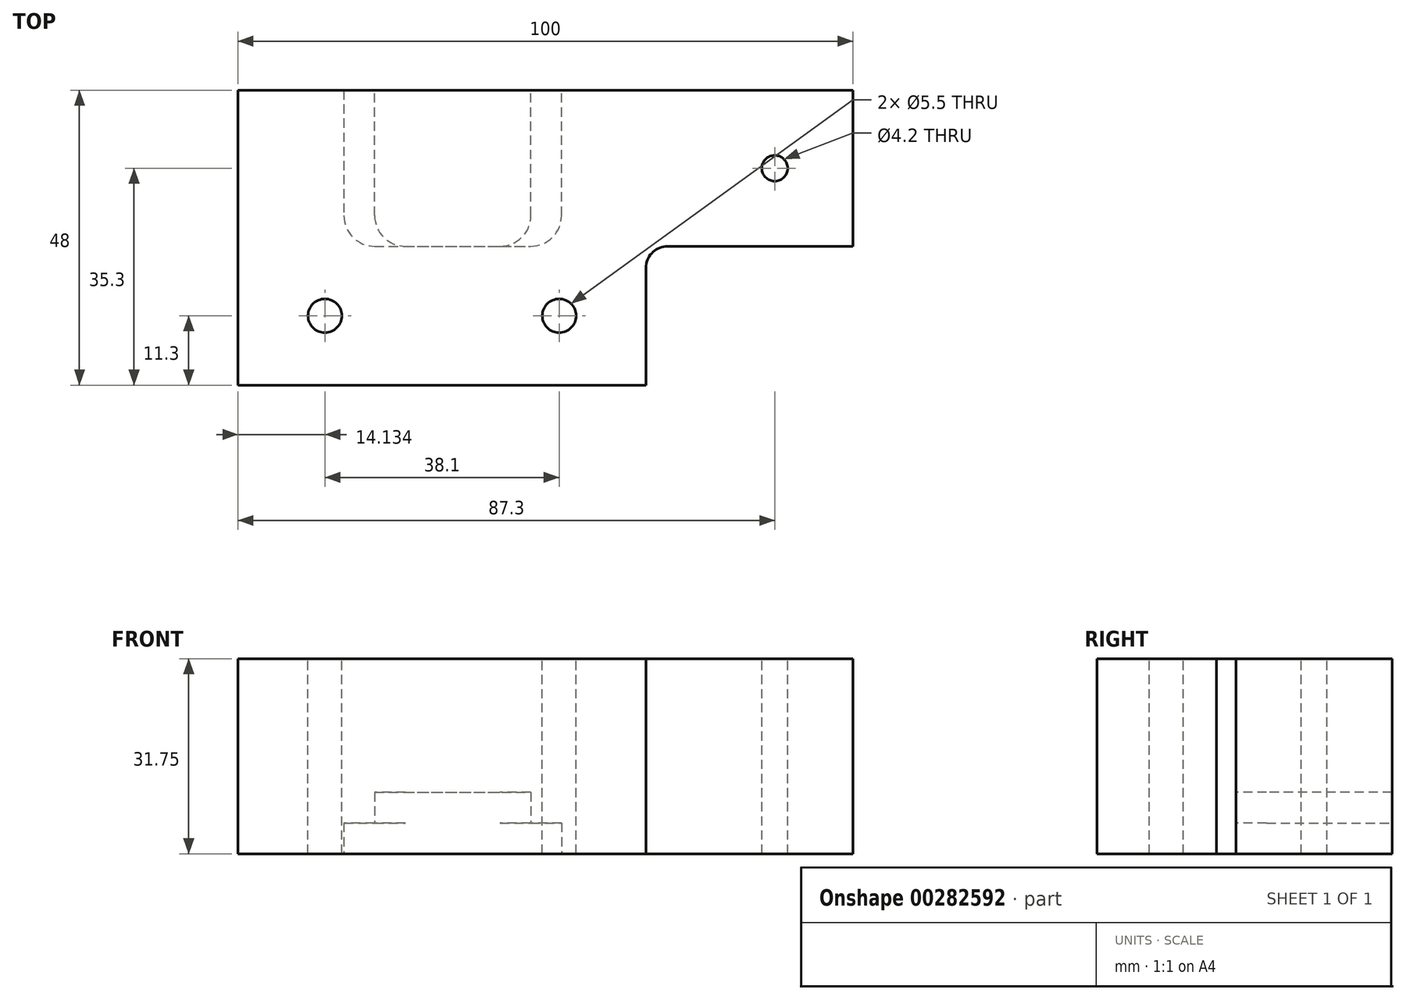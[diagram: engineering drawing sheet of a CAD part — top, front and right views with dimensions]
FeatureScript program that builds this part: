
annotation { "Feature Type Name" : "Feature", "Feature Type Description" : "" }
export const myFeature = defineFeature(function(context is Context, id is Id, definition is map)
    precondition{}
    {
        {
            var Q0;
            Q0=qCreatedBy(makeId("Top.planeOp"),FACE);
            var sketch = newSketch(context, id + "F0", { "sketchPlane" : qUnion([Q0])});
            skLineSegment(sketch, "E0.bottom", {"start": v(0, 0) * mm, "end": v(69.85, 0) * mm});
            skLineSegment(sketch, "E0.top", {"start": v(0, 48) * mm, "end": v(100, 48) * mm});
            skLineSegment(sketch, "E0.left", {"start": v(0, 0) * mm, "end": v(0, 48) * mm});
            skLineSegment(sketch, "E0.right", {"start": v(100, 22.6) * mm, "end": v(100, 48) * mm});
            skLineSegment(sketch, "E1", {"start": v(69.85, 22.6) * mm, "end": v(69.85, 0) * mm, "construction": true});
            skPoint(sketch, "E2.orphan", {"position": v(95.25, 0) * mm});
            skLineSegment(sketch, "E3", {"start": v(69.85, 22.6) * mm, "end": v(100, 22.6) * mm});
            skArc(sketch, "E4", {"start": v(69.85, 22.6) * mm, "mid": v(67.5, 21.7) * mm, "end": v(66.37, 19.45) * mm});
            skLineSegment(sketch, "E5", {"start": v(66.37, 19.45) * mm, "end": v(66.37, 0) * mm});
            skSolve(sketch);
        }
        {
            var Q0;
            Q0 = qSketchRegion(id + "F0", true);
            extrude(context, id + "F1", {"entities" : qUnion([Q0]), "depth" : 31.75 * mm});
        }
        {
            var Q0;
            Q0=makeQuery(id+"F1.opExtrude","CAP_FACE",FACE,{"disambiguationData":[OSD([sQuery(id+"F0.wireOp",EDGE,"E0.bottom"),sQuery(id+"F0.wireOp",EDGE,"E0.top"),sQuery(id+"F0.wireOp",EDGE,"E0.left"),sQuery(id+"F0.wireOp",EDGE,"E0.right"),sQuery(id+"F0.wireOp",EDGE,"ORaCKfpo-WbZt-Nzm5-LVTq-wue5MO5dMCIk"),sQuery(id+"F0.wireOp",EDGE,"E1")])],"isStart":true});
            var sketch = newSketch(context, id + "F2", { "sketchPlane" : qUnion([Q0])});
            skLineSegment(sketch, "E6.bottom", {"start": v(22.23, -48) * mm, "end": v(47.63, -48) * mm});
            skLineSegment(sketch, "E6.top", {"start": v(22.23, -22.6) * mm, "end": v(47.62, -22.6) * mm});
            skLineSegment(sketch, "E6.left", {"start": v(22.23, -48) * mm, "end": v(22.23, -22.6) * mm});
            skLineSegment(sketch, "E6.right", {"start": v(47.63, -48) * mm, "end": v(47.63, -22.6) * mm});
            skLineSegment(sketch, "E7", {"start": v(34.93, 0) * mm, "end": v(34.93, -48) * mm, "construction": true});
            skSolve(sketch);
        }
        {
            var Q0;
            Q0 = qSketchRegion(id + "F2", true);
            extrude(context, id + "F3", {"entities" : qUnion([Q0]), "operationType" : NewBodyOperationType.REMOVE, "oppositeDirection" : true, "depth" : 10 * mm});
        }
        {
            var Q0;
            Q0=makeQuery(id+"F3.boolean.opBoolean","COPY",EDGE,{"derivedFrom":makeQuery(id+"F3.opExtrude","SWEPT_EDGE",EDGE,{"disambiguationData":[OSD([sQuery(id+"F2.wireOp",EDGE,"E6.top"),sQuery(id+"F2.wireOp",EDGE,"E6.left")])]})});
            var Q1;
            Q1=makeQuery(id+"F3.boolean.opBoolean","COPY",EDGE,{"derivedFrom":makeQuery(id+"F3.opExtrude","SWEPT_EDGE",EDGE,{"disambiguationData":[OSD([sQuery(id+"F2.wireOp",EDGE,"E6.top"),sQuery(id+"F2.wireOp",EDGE,"E6.right")])]})});
            fillet(context, id + "F4", {"entities" : qUnion([Q0, Q1]), "radius" : 5 * mm, "tangentPropagation" : true, "allowEdgeOverflow" : false});
        }
        {
            var Q0;
            Q0=makeQuery(id+"F1.opExtrude","CAP_FACE",FACE,{"disambiguationData":[OSD([sQuery(id+"F0.wireOp",EDGE,"E0.bottom"),sQuery(id+"F0.wireOp",EDGE,"E0.top"),sQuery(id+"F0.wireOp",EDGE,"E0.left"),sQuery(id+"F0.wireOp",EDGE,"E0.right"),sQuery(id+"F0.wireOp",EDGE,"ORaCKfpo-WbZt-Nzm5-LVTq-wue5MO5dMCIk"),sQuery(id+"F0.wireOp",EDGE,"E1")])],"isStart":false});
            var sketch = newSketch(context, id + "F5", { "sketchPlane" : qUnion([Q0])});
            skLineSegment(sketch, "E8", {"start": v(0, 11.3) * mm, "end": v(69.85, 11.3) * mm, "construction": true});
            skLineSegment(sketch, "E9", {"start": v(33.18, 0) * mm, "end": v(33.18, 48) * mm, "construction": true});
            skPoint(sketch, "E9.endSnap0", {"position": v(50, 48) * mm});
            skPoint(sketch, "E10", {"position": v(14.13, 11.3) * mm});
            skPoint(sketch, "E11", {"position": v(52.23, 11.3) * mm});
            skPoint(sketch, "E12", {"position": v(33.18, 24) * mm});
            skSolve(sketch);
        }
        {
            var Q0;
            Q0=sQuery(id+"F5.wireOp",VERTEX,"E10");
            var Q1;
            Q1=sQuery(id+"F5.wireOp",VERTEX,"E11");
            var Q2;
            Q2=makeQuery(id+"F1.opExtrude","SWEPT_BODY",BODY,{"disambiguationData":[OSD([sQuery(id+"F0.wireOp",EDGE,"E0.bottom"),sQuery(id+"F0.wireOp",EDGE,"E0.top"),sQuery(id+"F0.wireOp",EDGE,"E0.left"),sQuery(id+"F0.wireOp",EDGE,"E0.right"),sQuery(id+"F0.wireOp",EDGE,"ORaCKfpo-WbZt-Nzm5-LVTq-wue5MO5dMCIk"),sQuery(id+"F0.wireOp",EDGE,"E1")])]});
            hole(context, id + "F6", {"style" : HoleStyle.SIMPLE, "endStyle" : HoleEndStyle.THROUGH, "standardTappedOrClearance" : lookupTablePath({ "standard" : "ISO", "fit" : "Normal", "size" : "M5", "type" : "Clearance" }), "standardBlindInLast" : lookupTablePath({ "fit" : "Standard", "standard" : "ISO", "size" : "M5", "type" : "Clearance" }), "holeDiameter" : 5.5 * mm, "tappedDepth" : 8.2 * mm, "tapClearance" : 3, "startFromSketch" : true, "locations" : qUnion([Q0, Q1]), "scope" : qUnion([Q2])});
        }
        {
            var Q0;
            Q0=makeQuery(id+"F1.opExtrude","CAP_FACE",FACE,{"disambiguationData":[OSD([sQuery(id+"F0.wireOp",EDGE,"E0.bottom"),sQuery(id+"F0.wireOp",EDGE,"E0.top"),sQuery(id+"F0.wireOp",EDGE,"E0.left"),sQuery(id+"F0.wireOp",EDGE,"E0.right"),sQuery(id+"F0.wireOp",EDGE,"ORaCKfpo-WbZt-Nzm5-LVTq-wue5MO5dMCIk"),sQuery(id+"F0.wireOp",EDGE,"E1")])],"isStart":false});
            var sketch = newSketch(context, id + "F7", { "sketchPlane" : qUnion([Q0])});
            skPoint(sketch, "E13", {"position": v(87.3, 35.3) * mm});
            skLineSegment(sketch, "E14", {"start": v(100, 22.6) * mm, "end": v(100, 48) * mm, "construction": true});
            skLineSegment(sketch, "E15", {"start": v(87.3, 35.3) * mm, "end": v(87.3, 38.48) * mm, "construction": true});
            skSolve(sketch);
        }
        {
            var Q0;
            Q0=sQuery(id+"F7.wireOp",VERTEX,"E13");
            var Q1;
            Q1=makeQuery(id+"F1.opExtrude","SWEPT_BODY",BODY,{"disambiguationData":[OSD([sQuery(id+"F0.wireOp",EDGE,"E0.bottom"),sQuery(id+"F0.wireOp",EDGE,"E0.top"),sQuery(id+"F0.wireOp",EDGE,"E0.left"),sQuery(id+"F0.wireOp",EDGE,"E0.right"),sQuery(id+"F0.wireOp",EDGE,"ORaCKfpo-WbZt-Nzm5-LVTq-wue5MO5dMCIk"),sQuery(id+"F0.wireOp",EDGE,"E1")])]});
            hole(context, id + "F8", {"style" : HoleStyle.SIMPLE, "endStyle" : HoleEndStyle.THROUGH, "standardTappedOrClearance" : lookupTablePath({ "standard" : "ISO", "engagement" : "75%", "pitch" : "0.8 mm", "size" : "M5", "type" : "Tapped" }), "standardBlindInLast" : lookupTablePath({ "standard" : "ISO", "engagement" : "75%", "pitch" : "0.8 mm", "size" : "M5", "type" : "Tapped" }), "holeDiameter" : 4.2 * mm, "showTappedDepth" : true, "tappedDepth" : 8.2 * mm, "tapClearance" : 3, "startFromSketch" : true, "locations" : qUnion([Q0]), "scope" : qUnion([Q1]), "majorDiameter" : 5 * mm});
        }
        {
            var Q0;
            Q0=makeQuery(id+"F1.opExtrude","CAP_FACE",FACE,{"disambiguationData":[OSD([sQuery(id+"F0.wireOp",EDGE,"E0.bottom"),sQuery(id+"F0.wireOp",EDGE,"E0.top"),sQuery(id+"F0.wireOp",EDGE,"E0.left"),sQuery(id+"F0.wireOp",EDGE,"E0.right"),sQuery(id+"F0.wireOp",EDGE,"E3"),sQuery(id+"F0.wireOp",EDGE,"E4"),sQuery(id+"F0.wireOp",EDGE,"E5")])],"isStart":true});
            var sketch = newSketch(context, id + "F9", { "sketchPlane" : qUnion([Q0])});
            skCircle(sketch, "E16", {"center": v(87.3, -35.3) * mm, "radius": 2.1 * mm});
            skCircle(sketch, "E17", {"center": v(52.23, -11.3) * mm, "radius": 2.75 * mm});
            skCircle(sketch, "E18", {"center": v(14.13, -11.3) * mm, "radius": 2.75 * mm});
            skLineSegment(sketch, "E19", {"start": v(47.63, -48) * mm, "end": v(47.63, -27.6) * mm});
            skLineSegment(sketch, "E20", {"start": v(47.63, -48) * mm, "end": v(100, -48) * mm});
            skLineSegment(sketch, "E21", {"start": v(100, -22.6) * mm, "end": v(100, -48) * mm});
            skLineSegment(sketch, "E22", {"start": v(69.85, -22.6) * mm, "end": v(100, -22.6) * mm});
            skArc(sketch, "E23", {"start": v(69.85, -22.6) * mm, "mid": v(67.5, -21.7) * mm, "end": v(66.37, -19.45) * mm});
            skLineSegment(sketch, "E24", {"start": v(66.37, -19.45) * mm, "end": v(66.37, 0) * mm});
            skLineSegment(sketch, "E25", {"start": v(0, 0) * mm, "end": v(66.37, 0) * mm});
            skLineSegment(sketch, "E26", {"start": v(0, 0) * mm, "end": v(0, -48) * mm});
            skLineSegment(sketch, "E27", {"start": v(0, -48) * mm, "end": v(22.23, -48) * mm});
            skLineSegment(sketch, "E28", {"start": v(22.23, -48) * mm, "end": v(22.23, -27.6) * mm});
            skArc(sketch, "E29", {"start": v(22.23, -27.6) * mm, "mid": v(23.69, -24.06) * mm, "end": v(27.23, -22.6) * mm});
            skLineSegment(sketch, "E30", {"start": v(27.23, -22.6) * mm, "end": v(42.63, -22.6) * mm});
            skArc(sketch, "E31", {"start": v(42.63, -22.6) * mm, "mid": v(46.16, -24.06) * mm, "end": v(47.63, -27.6) * mm});
            skLineSegment(sketch, "E32", {"start": v(34.93, -22.6) * mm, "end": v(34.93, -48) * mm, "construction": true});
            skLineSegment(sketch, "E33.0", {"start": v(22.23, -48) * mm, "end": v(47.63, -48) * mm, "construction": true});
            skSolve(sketch);
        }
        {
            var Q0;
            Q0=makeQuery(id+"F9.imprint","IMPRINT",FACE,{"disambiguationData":[TD([[makeQuery(id+"F9.imprint","IMPRINT",EDGE,{"derivedFrom":sQuery(id+"F9.wireOp",EDGE,"E16")}),-1.0]])]});
            var sketch = newSketch(context, id + "F10", { "sketchPlane" : qUnion([Q0])});
            skLineSegment(sketch, "E34.0", {"start": v(0, -48) * mm, "end": v(22.23, -48) * mm, "construction": true});
            skLineSegment(sketch, "E34.1", {"start": v(47.63, -48) * mm, "end": v(100, -48) * mm, "construction": true});
            skPoint(sketch, "E35.0", {"position": v(22.23, -27.6) * mm});
            skPoint(sketch, "E35.1", {"position": v(47.63, -27.6) * mm});
            skLineSegment(sketch, "E35.2", {"start": v(27.23, -22.6) * mm, "end": v(42.63, -22.6) * mm, "construction": true});
            skLineSegment(sketch, "E36", {"start": v(17.23, -48) * mm, "end": v(17.23, -27.6) * mm});
            skLineSegment(sketch, "E37", {"start": v(22.23, -22.6) * mm, "end": v(47.63, -22.6) * mm});
            skLineSegment(sketch, "E38", {"start": v(52.63, -27.6) * mm, "end": v(52.63, -48) * mm});
            skPoint(sketch, "E39.visualSharp", {"position": v(17.23, -22.6) * mm});
            skArc(sketch, "E39.filletArc", {"start": v(22.23, -22.6) * mm, "mid": v(18.69, -24.06) * mm, "end": v(17.23, -27.6) * mm});
            skPoint(sketch, "E40.visualSharp", {"position": v(52.63, -22.6) * mm});
            skArc(sketch, "E40.filletArc", {"start": v(52.63, -27.6) * mm, "mid": v(51.16, -24.06) * mm, "end": v(47.63, -22.6) * mm});
            skLineSegment(sketch, "E41", {"start": v(17.23, -48) * mm, "end": v(52.63, -48) * mm});
            skSolve(sketch);
        }
        {
            var Q0;
            Q0 = qSketchRegion(id + "F10", true);
            extrude(context, id + "F11", {"entities" : qUnion([Q0]), "operationType" : NewBodyOperationType.REMOVE, "oppositeDirection" : true, "depth" : 5 * mm});
        }
    });
